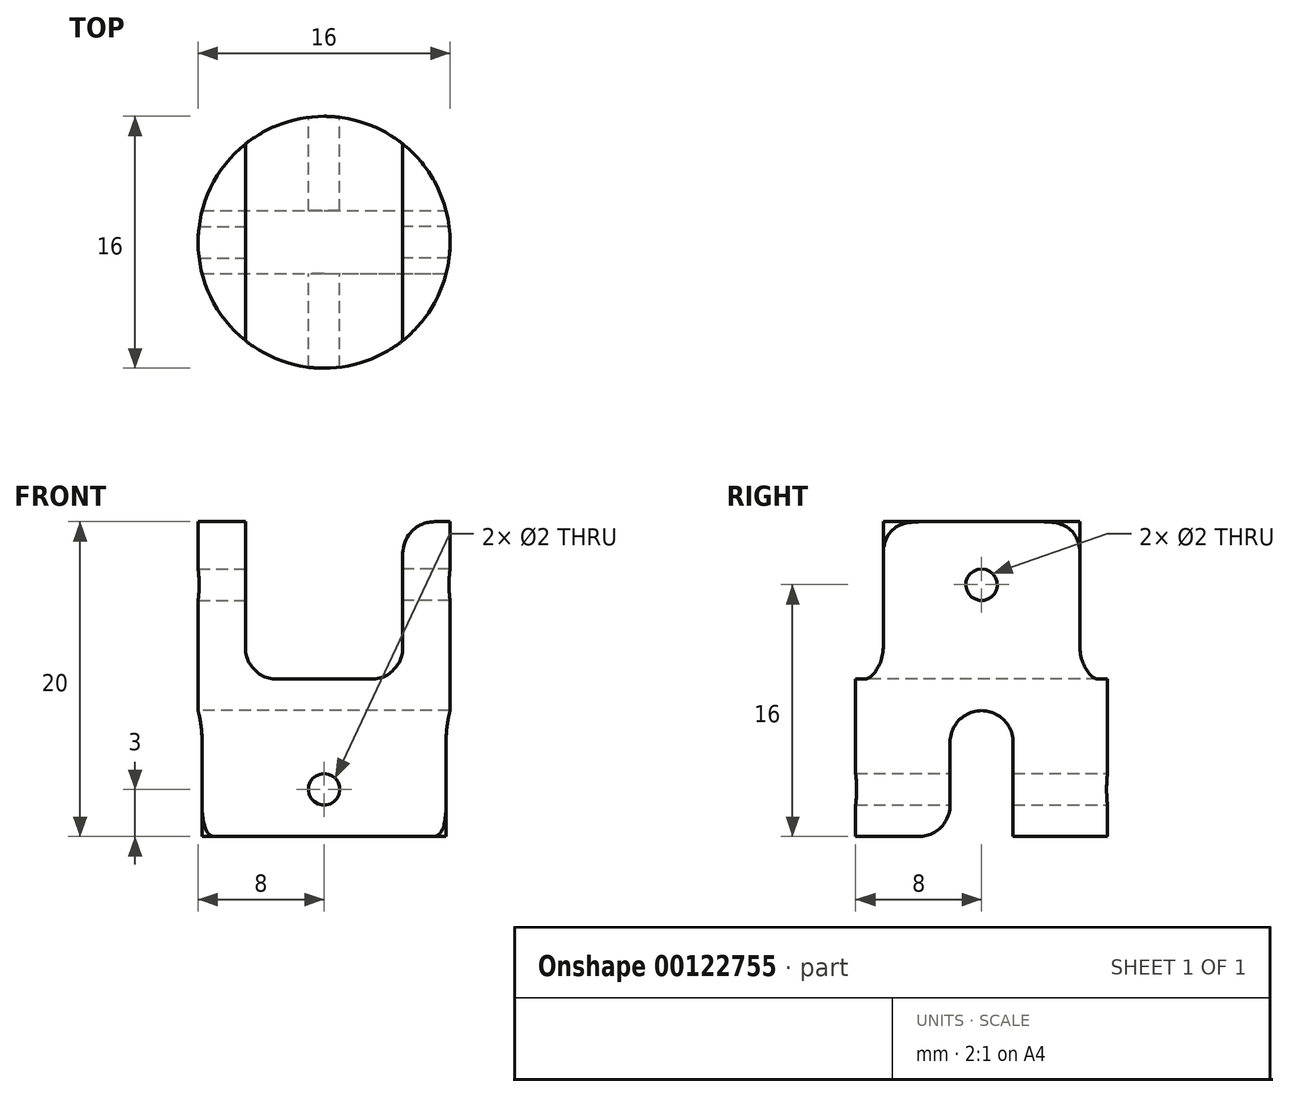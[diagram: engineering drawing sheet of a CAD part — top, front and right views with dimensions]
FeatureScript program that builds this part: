
annotation { "Feature Type Name" : "Feature", "Feature Type Description" : "" }
export const myFeature = defineFeature(function(context is Context, id is Id, definition is map)
    precondition{}
    {
        {
            var Q0;
            Q0=qCreatedBy(makeId("Top.planeOp"),FACE);
            var sketch = newSketch(context, id + "F0", { "sketchPlane" : qUnion([Q0])});
            skCircle(sketch, "E0", {"center": v(0, 0) * mm, "radius": 8 * mm});
            skSolve(sketch);
        }
        {
            var Q0;
            Q0=qSketchRegion(id+"F0",true);
            extrude(context, id + "F1", {"entities" : qUnion([Q0]), "endBound" : BoundingType.SYMMETRIC, "depth" : 20 * mm});
        }
        {
            var Q0;
            Q0=makeQuery(id+"F1.opExtrude","CAP_FACE",FACE,{"disambiguationData":[OSD([sQuery(id+"F0.wireOp",EDGE,"E0")])],"isStart":false});
            var sketch = newSketch(context, id + "F2", { "sketchPlane" : qUnion([Q0])});
            skLineSegment(sketch, "E1", {"start": v(-5, 6.24) * mm, "end": v(-5, -6.24) * mm});
            skLineSegment(sketch, "E2", {"start": v(5, 6.24) * mm, "end": v(5, -6.24) * mm});
            skSolve(sketch);
        }
        {
            var Q0;
            {var subQ0=sQuery(id+"F2.wireOp",EDGE,"E1");Q0=makeQuery(id+"F2.imprint","IMPRINT",FACE,{"disambiguationData":[TD([[makeQuery(id+"F2.imprint","IMPRINT",EDGE,{"derivedFrom":subQ0}),1.0]])]});}
            var Q1;
            Q1=qSketchRegion(id+"F4",true);
            extrude(context, id + "F3", {"entities" : qUnion([Q0, Q1]), "operationType" : NewBodyOperationType.REMOVE, "oppositeDirection" : true, "depth" : 10 * mm});
        }
        {
            var Q0;
            Q0=qCreatedBy(makeId("Right.planeOp"),FACE);
            var sketch = newSketch(context, id + "F4", { "sketchPlane" : qUnion([Q0])});
            skPoint(sketch, "E3", {"position": v(0, 6) * mm});
            skSolve(sketch);
        }
        {
            var Q0;
            Q0=sQuery(id+"F4.wireOp",VERTEX,"E3");
            var Q1;
            Q1=makeQuery(id+"F1.opExtrude","SWEPT_BODY",BODY,{"disambiguationData":[OSD([sQuery(id+"F0.wireOp",EDGE,"E0")])]});
            hole(context, id + "F5", {"style" : HoleStyle.SIMPLE, "endStyle" : HoleEndStyle.THROUGH, "holeDiameter" : 2 * mm, "locations" : qUnion([Q0]), "scope" : qUnion([Q1]), "isTappedThrough" : true});
        }
        {
            var Q0;
            Q0=sQuery(id+"F4.wireOp",VERTEX,"E3");
            var Q1;
            Q1=makeQuery(id+"F1.opExtrude","SWEPT_BODY",BODY,{"disambiguationData":[OSD([sQuery(id+"F0.wireOp",EDGE,"E0")])]});
            hole(context, id + "F6", {"style" : HoleStyle.SIMPLE, "endStyle" : HoleEndStyle.THROUGH, "oppositeDirection" : true, "holeDiameter" : 2 * mm, "locations" : qUnion([Q0]), "scope" : qUnion([Q1]), "isTappedThrough" : true});
        }
        {
            var Q0;
            Q0=makeQuery(id+"F3.boolean.opBoolean","COPY",EDGE,{"derivedFrom":makeQuery(id+"F3.opExtrude","CAP_EDGE",EDGE,{"disambiguationData":[OSD([sQuery(id+"F2.wireOp",EDGE,"E2")])],"isStart":true})});
            var Q1;
            Q1=makeQuery(id+"F3.boolean.opBoolean","COPY",EDGE,{"derivedFrom":makeQuery(id+"F3.opExtrude","CAP_EDGE",EDGE,{"disambiguationData":[OSD([sQuery(id+"F2.wireOp",EDGE,"E1")])],"isStart":true})});
            fillet(context, id + "F7", {"entities" : qUnion([Q0, Q1]), "radius" : 2 * mm, "tangentPropagation" : true, "allowEdgeOverflow" : false});
        }
        {
            var Q0;
            Q0=makeQuery(id+"F1.opExtrude","CAP_FACE",FACE,{"disambiguationData":[OSD([sQuery(id+"F0.wireOp",EDGE,"E0")])],"isStart":true});
            var sketch = newSketch(context, id + "F8", { "sketchPlane" : qUnion([Q0])});
            skLineSegment(sketch, "E4", {"start": v(-7.75, 2) * mm, "end": v(7.75, 2) * mm});
            skLineSegment(sketch, "E5", {"start": v(-7.75, -2) * mm, "end": v(7.75, -2) * mm});
            skSolve(sketch);
        }
        {
            var Q0;
            {var subQ0=sQuery(id+"F8.wireOp",EDGE,"E4");Q0=makeQuery(id+"F8.imprint","IMPRINT",FACE,{"disambiguationData":[TD([[makeQuery(id+"F8.imprint","IMPRINT",EDGE,{"derivedFrom":subQ0}),-1.0]])]});}
            extrude(context, id + "F9", {"entities" : qUnion([Q0]), "operationType" : NewBodyOperationType.REMOVE, "oppositeDirection" : true, "depth" : 8 * mm});
        }
        {
            var Q0;
            Q0=makeQuery(id+"F9.boolean.opBoolean","COPY",EDGE,{"derivedFrom":makeQuery(id+"F9.opExtrude","CAP_EDGE",EDGE,{"disambiguationData":[OSD([sQuery(id+"F8.wireOp",EDGE,"E5")])],"isStart":true})});
            var Q1;
            Q1=makeQuery(id+"F9.boolean.opBoolean","COPY",EDGE,{"derivedFrom":makeQuery(id+"F9.opExtrude","CAP_EDGE",EDGE,{"disambiguationData":[OSD([sQuery(id+"F8.wireOp",EDGE,"E4")])],"isStart":true})});
            var Q2;
            Q2=makeQuery(id+"F9.boolean.opBoolean","COPY",EDGE,{"derivedFrom":makeQuery(id+"F9.opExtrude","CAP_EDGE",EDGE,{"disambiguationData":[OSD([sQuery(id+"F8.wireOp",EDGE,"E4")])],"isStart":false})});
            var Q3;
            Q3=makeQuery(id+"F9.boolean.opBoolean","COPY",EDGE,{"derivedFrom":makeQuery(id+"F9.opExtrude","CAP_EDGE",EDGE,{"disambiguationData":[OSD([sQuery(id+"F8.wireOp",EDGE,"E5")])],"isStart":false})});
            var Q4;
            Q4=makeQuery(id+"F3.boolean.opBoolean","COPY",EDGE,{"derivedFrom":makeQuery(id+"F3.opExtrude","CAP_EDGE",EDGE,{"disambiguationData":[OSD([sQuery(id+"F2.wireOp",EDGE,"E1")])],"isStart":false})});
            var Q5;
            Q5=makeQuery(id+"F3.boolean.opBoolean","COPY",EDGE,{"derivedFrom":makeQuery(id+"F3.opExtrude","CAP_EDGE",EDGE,{"disambiguationData":[OSD([sQuery(id+"F2.wireOp",EDGE,"E2")])],"isStart":false})});
            fillet(context, id + "F10", {"entities" : qUnion([Q0, Q1, Q2, Q3, Q4, Q5]), "radius" : 2 * mm, "tangentPropagation" : true, "allowEdgeOverflow" : false});
        }
        {
            var Q0;
            Q0=qCreatedBy(makeId("Front.planeOp"),FACE);
            var sketch = newSketch(context, id + "F11", { "sketchPlane" : qUnion([Q0])});
            skCircle(sketch, "E6", {"center": v(0, -7) * mm, "radius": 1 * mm});
            skSolve(sketch);
        }
        {
            var Q0;
            Q0=makeQuery(id+"F11.imprint","IMPRINT",FACE,{"disambiguationData":[TD([[makeQuery(id+"F11.imprint","IMPRINT",EDGE,{"derivedFrom":sQuery(id+"F11.wireOp",EDGE,"E6")}),1.0]])]});
            extrude(context, id + "F12", {"entities" : qUnion([Q0]), "operationType" : NewBodyOperationType.REMOVE, "endBound" : BoundingType.SYMMETRIC, "depth" : 16 * mm});
        }
    });
